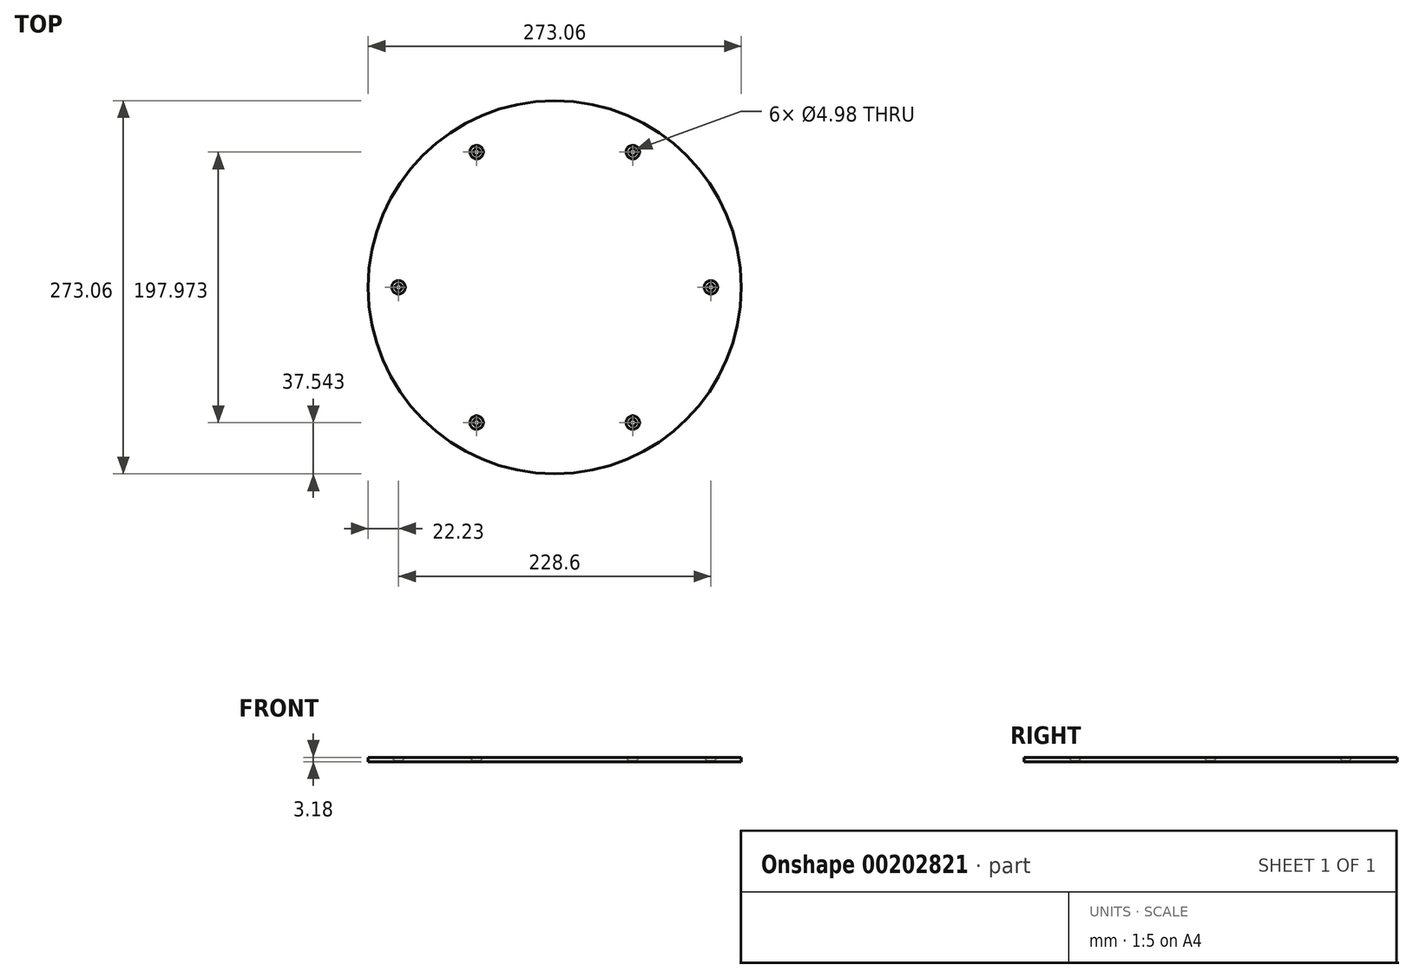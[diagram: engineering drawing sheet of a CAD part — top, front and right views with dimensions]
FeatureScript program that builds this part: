
annotation { "Feature Type Name" : "Feature", "Feature Type Description" : "" }
export const myFeature = defineFeature(function(context is Context, id is Id, definition is map)
    precondition{}
    {
        {
            var Q0;
            Q0=qCreatedBy(makeId("Top.planeOp"),FACE);
            var sketch = newSketch(context, id + "F0", { "sketchPlane" : qUnion([Q0])});
            skCircle(sketch, "E0", {"center": v(0, 0) * mm, "radius": 136.53 * mm});
            skSolve(sketch);
        }
        {
            var Q0;
            Q0 = qSketchRegion(id + "F0", true);
            extrude(context, id + "F1", {"entities" : qUnion([Q0]), "oppositeDirection" : true, "depth" : 3.17 * mm});
        }
        {
            var Q0;
            Q0=makeQuery(id+"F1.opExtrude","CAP_FACE",FACE,{"disambiguationData":[OSD([sQuery(id+"F0.wireOp",EDGE,"E0")])],"isStart":true});
            var sketch = newSketch(context, id + "F2", { "sketchPlane" : qUnion([Q0])});
            skCircle(sketch, "E1", {"center": v(0, 0) * mm, "radius": 114.3 * mm, "construction": true});
            skPoint(sketch, "E2", {"position": v(-114.3, 0) * mm});
            skPoint(sketch, "E3.1.0", {"position": v(-57.15, -98.99) * mm});
            skPoint(sketch, "E3.2.0", {"position": v(57.15, -98.99) * mm});
            skPoint(sketch, "E3.3.0", {"position": v(114.3, 0) * mm});
            skPoint(sketch, "E3.4.0", {"position": v(57.15, 98.99) * mm});
            skPoint(sketch, "E3.5.0", {"position": v(-57.15, 98.99) * mm});
            skSolve(sketch);
        }
        {
            var Q0;
            Q0=sQuery(id+"F2.wireOp",VERTEX,"E2");
            var Q1;
            Q1=sQuery(id+"F2.wireOp",VERTEX,"E3.5.0");
            var Q2;
            Q2=sQuery(id+"F2.wireOp",VERTEX,"E3.4.0");
            var Q3;
            Q3=sQuery(id+"F2.wireOp",VERTEX,"E3.3.0");
            var Q4;
            Q4=sQuery(id+"F2.wireOp",VERTEX,"E3.2.0");
            var Q5;
            Q5=sQuery(id+"F2.wireOp",VERTEX,"E3.1.0");
            var Q6;
            Q6=makeQuery(id+"F1.opExtrude","SWEPT_BODY",BODY,{"disambiguationData":[OSD([sQuery(id+"F0.wireOp",EDGE,"E0")])]});
            hole(context, id + "F3", {"style" : HoleStyle.C_SINK, "endStyle" : HoleEndStyle.THROUGH, "holeDiameter" : 4.98 * mm, "cSinkDiameter" : 9.83 * mm, "cSinkAngle" : 82 * degree, "startFromSketch" : true, "locations" : qUnion([Q0, Q1, Q2, Q3, Q4, Q5]), "scope" : qUnion([Q6]), "isTappedThrough" : true});
        }
    });
